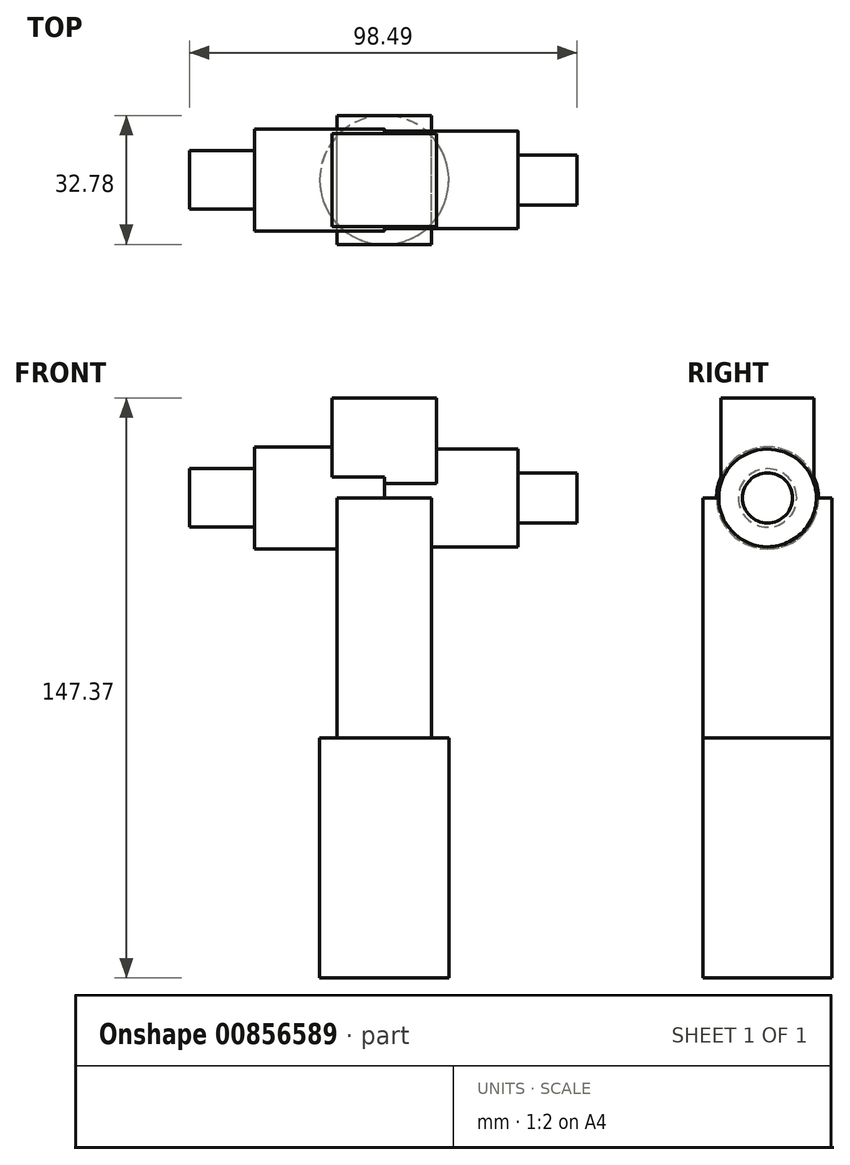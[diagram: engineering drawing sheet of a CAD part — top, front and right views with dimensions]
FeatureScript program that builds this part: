
annotation { "Feature Type Name" : "Feature", "Feature Type Description" : "" }
export const myFeature = defineFeature(function(context is Context, id is Id, definition is map)
    precondition{}
    {
        {
            var Q0;
            Q0=qCreatedBy(makeId("Right.planeOp"),FACE);
            var sketch = newSketch(context, id + "F0", { "sketchPlane" : qUnion([Q0])});
            skCircle(sketch, "E0", {"center": v(0, 0) * mm, "radius": 12.4 * mm});
            skSolve(sketch);
        }
        {
            var Q0;
            Q0 = qSketchRegion(id + "F0", true);
            extrude(context, id + "F1", {"entities" : qUnion([Q0]), "depth" : 34 * mm, "offsetDistance" : 25.4 * mm});
        }
        {
            var Q0;
            Q0=qCreatedBy(makeId("Right.planeOp"),FACE);
            var sketch = newSketch(context, id + "F2", { "sketchPlane" : qUnion([Q0])});
            skCircle(sketch, "E1", {"center": v(0, 0) * mm, "radius": 12.95 * mm});
            skSolve(sketch);
        }
        {
            var Q0;
            Q0 = qSketchRegion(id + "F2", true);
            extrude(context, id + "F3", {"entities" : qUnion([Q0]), "operationType" : NewBodyOperationType.ADD, "oppositeDirection" : true, "depth" : 32.93 * mm, "offsetDistance" : 25.4 * mm});
        }
        {
            var Q0;
            Q0=qCreatedBy(makeId("Top.planeOp"),FACE);
            var sketch = newSketch(context, id + "F4", { "sketchPlane" : qUnion([Q0])});
            skLineSegment(sketch, "E2.bottom", {"start": v(-13.28, -11.83) * mm, "end": v(13.28, -11.83) * mm});
            skLineSegment(sketch, "E2.top", {"start": v(-13.28, 11.83) * mm, "end": v(13.28, 11.83) * mm});
            skLineSegment(sketch, "E2.left", {"start": v(-13.28, -11.83) * mm, "end": v(-13.28, 11.83) * mm});
            skLineSegment(sketch, "E2.right", {"start": v(13.28, -11.83) * mm, "end": v(13.28, 11.83) * mm});
            skPoint(sketch, "E2.middle", {"position": v(0, 0) * mm});
            skSolve(sketch);
        }
        {
            var Q0;
            Q0=qCreatedBy(makeId("Top.planeOp"),FACE);
            var sketch = newSketch(context, id + "F5", { "sketchPlane" : qUnion([Q0])});
            skLineSegment(sketch, "E3.bottom", {"start": v(12.03, -16.39) * mm, "end": v(-12.03, -16.39) * mm});
            skLineSegment(sketch, "E3.top", {"start": v(12.03, 16.39) * mm, "end": v(-12.03, 16.39) * mm});
            skLineSegment(sketch, "E3.left", {"start": v(12.03, -16.39) * mm, "end": v(12.03, 16.39) * mm});
            skLineSegment(sketch, "E3.right", {"start": v(-12.03, -16.39) * mm, "end": v(-12.03, 16.39) * mm});
            skPoint(sketch, "E3.middle", {"position": v(0, 0) * mm});
            skSolve(sketch);
        }
        {
            var Q0;
            Q0=makeQuery(id+"F5.imprint","IMPRINT",FACE,{"disambiguationData":[TD([[makeQuery(id+"F5.imprint","IMPRINT",EDGE,{"derivedFrom":sQuery(id+"F5.wireOp",EDGE,"E3.bottom")}),-1.0]])]});
            extrude(context, id + "F6", {"entities" : qUnion([Q0]), "operationType" : NewBodyOperationType.ADD, "oppositeDirection" : true, "depth" : 60.95 * mm, "offsetDistance" : 25.4 * mm});
        }
        {
            var Q0;
            Q0=makeQuery(id+"F1.opExtrude","CAP_FACE",FACE,{"disambiguationData":[OSD([sQuery(id+"F0.wireOp",EDGE,"E0")])],"isStart":false});
            var sketch = newSketch(context, id + "F7", { "sketchPlane" : qUnion([Q0])});
            skCircle(sketch, "E4", {"center": v(0, 0) * mm, "radius": 6.34 * mm});
            skSolve(sketch);
        }
        {
            var Q0;
            Q0 = qSketchRegion(id + "F4", true);
            extrude(context, id + "F8", {"entities" : qUnion([Q0]), "operationType" : NewBodyOperationType.ADD, "depth" : 25.4 * mm, "offsetDistance" : 25.4 * mm});
        }
        {
            var Q0;
            Q0 = qSketchRegion(id + "F7", true);
            extrude(context, id + "F9", {"entities" : qUnion([Q0]), "operationType" : NewBodyOperationType.ADD, "depth" : 14.98 * mm, "offsetDistance" : 25.4 * mm});
        }
        {
            var Q0;
            Q0=makeQuery(id+"F3.opExtrude","CAP_FACE",FACE,{"disambiguationData":[OSD([sQuery(id+"F2.wireOp",EDGE,"E1")])],"isStart":false});
            var sketch = newSketch(context, id + "F10", { "sketchPlane" : qUnion([Q0])});
            skCircle(sketch, "E5", {"center": v(0, 0) * mm, "radius": 7.43 * mm});
            skSolve(sketch);
        }
        {
            var Q0;
            Q0 = qSketchRegion(id + "F10", true);
            extrude(context, id + "F11", {"entities" : qUnion([Q0]), "operationType" : NewBodyOperationType.ADD, "depth" : 16.59 * mm, "offsetDistance" : 25.4 * mm});
        }
        {
            var Q0;
            Q0=makeQuery(id+"F6.opExtrude","CAP_FACE",FACE,{"disambiguationData":[OSD([sQuery(id+"F5.wireOp",EDGE,"E3.bottom"),sQuery(id+"F5.wireOp",EDGE,"E3.top"),sQuery(id+"F5.wireOp",EDGE,"E3.left"),sQuery(id+"F5.wireOp",EDGE,"E3.right")])],"isStart":false});
            var sketch = newSketch(context, id + "F12", { "sketchPlane" : qUnion([Q0])});
            skCircle(sketch, "E6", {"center": v(0, 0) * mm, "radius": 16.39 * mm});
            skSolve(sketch);
        }
        {
            var Q0;
            {var subQ0=sQuery(id+"F12.wireOp",EDGE,"E6");var subQ7=makeQuery(id+"F12.imprint","INTERSECT",VERTEX,{"derivedFrom":[makeQuery(id+"F6.opExtrude","CAP_EDGE",EDGE,{"disambiguationData":[OSD([sQuery(id+"F5.wireOp",EDGE,"E3.bottom")])],"isStart":false}),subQ0]});Q0=makeQuery(id+"F12.imprint","IMPRINT",FACE,{"disambiguationData":[TD([[makeQuery(id+"F12.imprint","IMPRINT",EDGE,{"disambiguationData":[TD([[subQ7,1.0]])],"derivedFrom":subQ0}),1.0]])]});}
            var Q1;
            Q1 = qSketchRegion(id + "F12", true);
            extrude(context, id + "F13", {"entities" : qUnion([Q0, Q1]), "operationType" : NewBodyOperationType.ADD, "depth" : 61.03 * mm, "offsetDistance" : 25.4 * mm});
        }
    });
